SOLIDWORKS PART (.sldprt)
format: sldprt  version: not decoded by parser v0  size: 243,712 bytes
history: native  units: mm
features: sketch x8, extrude x5, fillet x4, plane x3, cut_extrude x3, material x1 (+8 scaffold rows collapsed)
feature tree (32):
  scaffold x8  (default folders/planes/origin — collapsed)
  material  "Matériau <non spécifié>"
  plane  "Face"
  plane  "Dessus"
  plane  "Droite"
  sketch  "Esquisse1"  dims[D1=1.0mm D2=0.94mm]
  extrude  "Base-Extrusion"  Depth=0.5mm
  sketch  "Esquisse2"
  extrude  "Boss.-Extru.1"  Depth=5.02mm
  sketch  "Esquisse3"
  cut_extrude  "Enlèv. mat.-Extru.1"  Depth=0.5mm
  sketch  "Esquisse4"
  extrude  "Boss.-Extru.2"  Depth=4mm
  sketch  "Esquisse5"
  cut_extrude  "Enlèv. mat.-Extru.2"  [1 undecoded]
  fillet  "Congé1"  Radius=0.1mm
  sketch  "Esquisse6"  dims[D1=0.225mm D2=0.225mm D3=0.225mm D4=0.225mm]
  extrude  "Boss.-Extru.3"  Depth=3.8mm
  fillet  "Congé2"  Radius=0.95mm
  sketch  "Esquisse7"  dims[D1=~0.335412mm]
  cut_extrude  "Enlèv. mat.-Extru.3"  [1 undecoded]
  sketch  "Esquisse8"
  extrude  "Boss.-Extru.4"  Depth=0.5mm
  fillet  "Congé3"  Radius=0.5mm
  fillet  "Congé4"  Radius=0.2mm
decode coverage: 13 of 20 modeling features carry decoded parameters
note: ~ marks probable driven/reference dimensions
note: 2 parameter values undecoded
note: suppression state not decoded; provenance and decode notes live in map.json
